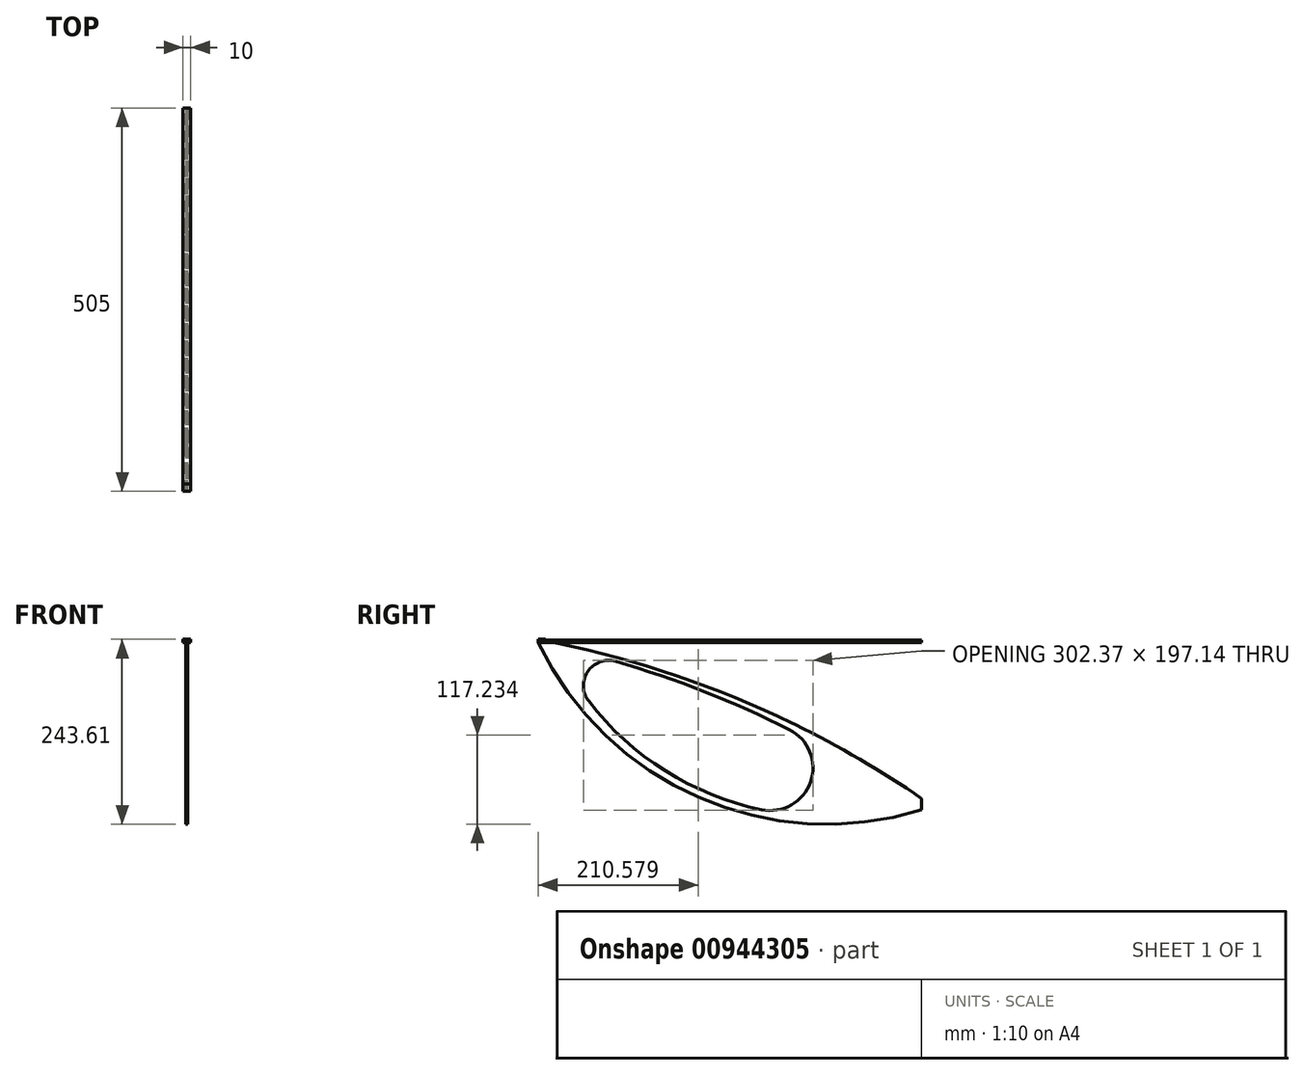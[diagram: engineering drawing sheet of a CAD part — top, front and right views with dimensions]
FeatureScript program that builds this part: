
annotation { "Feature Type Name" : "Feature", "Feature Type Description" : "" }
export const myFeature = defineFeature(function(context is Context, id is Id, definition is map)
    precondition{}
    {
        {
            var Q0;
            Q0=qCreatedBy(makeId("Front.planeOp"),FACE);
            var sketch = newSketch(context, id + "F0", { "sketchPlane" : qUnion([Q0])});
            skLineSegment(sketch, "E0", {"start": v(-5, -10.74) * mm, "end": v(5, -10.74) * mm});
            skLineSegment(sketch, "E1", {"start": v(-5, -7.74) * mm, "end": v(5, -7.74) * mm});
            skLineSegment(sketch, "E2", {"start": v(-5, -7.74) * mm, "end": v(-5, -10.74) * mm});
            skLineSegment(sketch, "E3", {"start": v(5, -7.74) * mm, "end": v(5, -10.74) * mm});
            skSolve(sketch);
        }
        {
            var Q0;
            Q0=makeQuery(id+"F0.imprint","IMPRINT",FACE,{"disambiguationData":[TD([[makeQuery(id+"F0.imprint","IMPRINT",EDGE,{"derivedFrom":sQuery(id+"F0.wireOp",EDGE,"E0")}),1.0]])]});
            var Q1;
            Q1=sQuery(id+"F0.wireOp",EDGE,"E0");
            extrude(context, id + "F1", {"entities" : qUnion([Q0]), "surfaceEntities" : qUnion([Q1]), "depth" : 505 * mm, "offsetDistance" : 25 * mm});
        }
        {
            var Q0;
            Q0=qCreatedBy(makeId("Right.planeOp"),FACE);
            var sketch = newSketch(context, id + "F2", { "sketchPlane" : qUnion([Q0])});
            skArc(sketch, "E4", {"start": v(0, -231.42) * mm, "mid": v(-240.85, -94.43) * mm, "end": v(-505, -10.74) * mm});
            skArc(sketch, "E5", {"start": v(0, -216.42) * mm, "mid": v(-81.58, -164.8) * mm, "end": v(-166.7, -119.23) * mm});
            skLineSegment(sketch, "E6", {"start": v(0, -216.42) * mm, "end": v(0, -231.42) * mm});
            skLineSegment(sketch, "E7", {"start": v(-505, -10.74) * mm, "end": v(-485, -10.74) * mm});
            skLineSegment(sketch, "E8", {"start": v(-170.9, -117.19) * mm, "end": v(-7.33, -10.74) * mm});
            skLineSegment(sketch, "E9", {"start": v(-166.7, -119.23) * mm, "end": v(0, -10.74) * mm});
            skArc(sketch, "E10.trimOffspring", {"start": v(-170.9, -117.19) * mm, "mid": v(-324.61, -54.13) * mm, "end": v(-485, -10.74) * mm});
            skLineSegment(sketch, "E11", {"start": v(0, -10.74) * mm, "end": v(-7.33, -10.74) * mm});
            skPoint(sketch, "E12.orphan", {"position": v(9.17, 0) * mm});
            skLineSegment(sketch, "E13.direction1", {"start": v(-751.48, -1313.77) * mm, "end": v(-726.48, -1313.77) * mm, "construction": true});
            skArc(sketch, "E14.2.0.0", {"start": v(-129.66, -90.36) * mm, "mid": v(-263.2, -43.28) * mm, "end": v(-401, -10.74) * mm});
            skArc(sketch, "E14.2.0.1", {"start": v(-140.93, -97.69) * mm, "mid": v(-281.01, -46.17) * mm, "end": v(-426, -10.74) * mm});
            skArc(sketch, "E15.1.0.0", {"start": v(-119.99, -84.06) * mm, "mid": v(-246.15, -40.95) * mm, "end": v(-376, -10.74) * mm});
            skArc(sketch, "E15.1.0.1", {"start": v(-129.66, -90.36) * mm, "mid": v(-252.57, -46.24) * mm, "end": v(-379.22, -14.45) * mm});
            skArc(sketch, "E15.2.0.0", {"start": v(-110.86, -78.12) * mm, "mid": v(-219.51, -41.32) * mm, "end": v(-330.94, -14.06) * mm});
            skArc(sketch, "E15.2.0.1", {"start": v(-119.99, -84.06) * mm, "mid": v(-235.47, -43.83) * mm, "end": v(-354.18, -14.43) * mm});
            skArc(sketch, "E16.1.0.0", {"start": v(-110.86, -78.12) * mm, "mid": v(-231.58, -35.17) * mm, "end": v(-355.89, -4.09) * mm});
            skArc(sketch, "E17.trimOffspring", {"start": v(-140.93, -97.69) * mm, "mid": v(-277.94, -46.87) * mm, "end": v(-419.72, -11.46) * mm});
            skArc(sketch, "E18.trimOffspring", {"start": v(-78.26, -56.9) * mm, "mid": v(-137.96, -36.17) * mm, "end": v(-198.58, -18.3) * mm});
            skArc(sketch, "E19.trimOffspring", {"start": v(-69.13, -50.96) * mm, "mid": v(-122.21, -33.15) * mm, "end": v(-176, -17.61) * mm});
            skPoint(sketch, "E20.orphan", {"position": v(-226.82, -11.3) * mm});
            skPoint(sketch, "E21.orphan", {"position": v(-178.33, -10.54) * mm});
            skPoint(sketch, "E22.orphan", {"position": v(-151.85, -10.94) * mm});
            skLineSegment(sketch, "E23", {"start": v(-451, -10.74) * mm, "end": v(-476, -10.74) * mm});
            skLineSegment(sketch, "E24", {"start": v(-426, -10.74) * mm, "end": v(-401, -10.74) * mm});
            skLineSegment(sketch, "E25", {"start": v(-376, -10.74) * mm, "end": v(-330.94, -14.06) * mm});
            skLineSegment(sketch, "E26", {"start": v(-151.85, -10.94) * mm, "end": v(-52.05, -39.84) * mm});
            skLineSegment(sketch, "E27", {"start": v(-178.33, -10.54) * mm, "end": v(-59.78, -44.87) * mm});
            skLineSegment(sketch, "E28.1.0.0", {"start": v(-197.9, -117.19) * mm, "end": v(-195.2, -115.43) * mm});
            skLineSegment(sketch, "E28.1.0.1", {"start": v(-193.7, -119.23) * mm, "end": v(-190.56, -117.19) * mm});
            skLineSegment(sketch, "E28.2.0.0", {"start": v(-202.27, -102.46) * mm, "end": v(-173.78, -83.92) * mm});
            skLineSegment(sketch, "E28.2.0.1", {"start": v(-197.96, -104.43) * mm, "end": v(-169.26, -85.75) * mm});
            skLineSegment(sketch, "E28.3.0.0", {"start": v(-218.3, -95.32) * mm, "end": v(-190.57, -77.28) * mm});
            skLineSegment(sketch, "E28.3.0.1", {"start": v(-213.92, -97.25) * mm, "end": v(-185.99, -79.07) * mm});
            skLineSegment(sketch, "E28.4.0.0", {"start": v(-234.56, -88.33) * mm, "end": v(-207.62, -70.8) * mm});
            skLineSegment(sketch, "E28.4.0.1", {"start": v(-230.12, -90.22) * mm, "end": v(-202.97, -72.54) * mm});
            skLineSegment(sketch, "E28.5.0.0", {"start": v(-251.06, -81.5) * mm, "end": v(-224.94, -64.5) * mm});
            skLineSegment(sketch, "E28.5.0.1", {"start": v(-246.56, -83.34) * mm, "end": v(-220.2, -66.2) * mm});
            skLineSegment(sketch, "E28.6.0.0", {"start": v(-267.81, -74.83) * mm, "end": v(-242.53, -58.37) * mm});
            skLineSegment(sketch, "E28.6.0.1", {"start": v(-263.24, -76.63) * mm, "end": v(-237.72, -60.02) * mm});
            skLineSegment(sketch, "E28.7.0.0", {"start": v(-284.82, -68.33) * mm, "end": v(-260.4, -52.43) * mm});
            skLineSegment(sketch, "E28.7.0.1", {"start": v(-280.18, -70.08) * mm, "end": v(-255.51, -54.03) * mm});
            skLineSegment(sketch, "E28.8.0.0", {"start": v(-302.09, -62) * mm, "end": v(-278.56, -46.68) * mm});
            skLineSegment(sketch, "E28.8.0.1", {"start": v(-297.37, -63.7) * mm, "end": v(-273.6, -48.22) * mm});
            skLineSegment(sketch, "E28.9.0.0", {"start": v(-319.62, -55.84) * mm, "end": v(-297.02, -41.13) * mm});
            skLineSegment(sketch, "E28.9.0.1", {"start": v(-314.83, -57.5) * mm, "end": v(-291.98, -42.62) * mm});
            skLineSegment(sketch, "E28.10.0.0", {"start": v(-337.44, -49.86) * mm, "end": v(-315.8, -35.78) * mm});
            skLineSegment(sketch, "E28.10.0.1", {"start": v(-332.57, -51.46) * mm, "end": v(-310.67, -37.2) * mm});
            skLineSegment(sketch, "E28.11.0.0", {"start": v(-355.55, -44.07) * mm, "end": v(-334.9, -30.64) * mm});
            skLineSegment(sketch, "E28.11.0.1", {"start": v(-350.6, -45.62) * mm, "end": v(-329.69, -32.01) * mm});
            skLineSegment(sketch, "E28.12.0.0", {"start": v(-373.95, -38.48) * mm, "end": v(-354.36, -25.72) * mm});
            skLineSegment(sketch, "E28.12.0.1", {"start": v(-368.92, -39.98) * mm, "end": v(-349.04, -27.04) * mm});
            skLineSegment(sketch, "E28.13.0.0", {"start": v(-392.67, -33.09) * mm, "end": v(-374.16, -21.04) * mm});
            skLineSegment(sketch, "E28.13.0.1", {"start": v(-387.55, -34.53) * mm, "end": v(-368.74, -22.29) * mm});
            skLineSegment(sketch, "E28.14.0.0", {"start": v(-411.7, -27.9) * mm, "end": v(-394.33, -16.6) * mm});
            skLineSegment(sketch, "E28.14.0.1", {"start": v(-406.5, -29.29) * mm, "end": v(-388.81, -17.78) * mm});
            skLineSegment(sketch, "E28.15.0.0", {"start": v(-431.08, -22.94) * mm, "end": v(-414.88, -12.4) * mm});
            skLineSegment(sketch, "E28.15.0.1", {"start": v(-425.78, -24.27) * mm, "end": v(-409.26, -13.51) * mm});
            skLineSegment(sketch, "E28.16.0.0", {"start": v(-450.8, -18.2) * mm, "end": v(-439.33, -10.74) * mm});
            skLineSegment(sketch, "E28.16.0.1", {"start": v(-445.4, -19.47) * mm, "end": v(-432, -10.74) * mm});
            skLineSegment(sketch, "E28.direction1", {"start": v(-170.9, -117.19) * mm, "end": v(-197.9, -117.19) * mm, "construction": true});
            skLineSegment(sketch, "E29.trimOffspring", {"start": v(-186.47, -109.75) * mm, "end": v(-157.23, -90.73) * mm});
            skLineSegment(sketch, "E30.trimOffspring", {"start": v(-182.22, -111.76) * mm, "end": v(-152.78, -92.6) * mm});
            skLineSegment(sketch, "E31.trimOffspring", {"start": v(-233.19, -52.3) * mm, "end": v(-225.02, -46.98) * mm});
            skLineSegment(sketch, "E32.trimOffspring", {"start": v(-228.29, -53.88) * mm, "end": v(-220.05, -48.52) * mm});
            skLineSegment(sketch, "E33.trimOffspring", {"start": v(-215.25, -58.2) * mm, "end": v(-206.81, -52.7) * mm});
            skLineSegment(sketch, "E34.trimOffspring", {"start": v(-210.43, -59.83) * mm, "end": v(-201.92, -54.3) * mm});
            skLineSegment(sketch, "E35.trimOffspring", {"start": v(-197.6, -64.28) * mm, "end": v(-188.9, -58.62) * mm});
            skLineSegment(sketch, "E36.trimOffspring", {"start": v(-192.86, -65.97) * mm, "end": v(-184.08, -60.26) * mm});
            skLineSegment(sketch, "E37.trimOffspring", {"start": v(-180.23, -70.54) * mm, "end": v(-171.27, -64.72) * mm});
            skLineSegment(sketch, "E38.trimOffspring", {"start": v(-175.55, -72.28) * mm, "end": v(-166.53, -66.4) * mm});
            skLineSegment(sketch, "E39.trimOffspring", {"start": v(-158.51, -78.76) * mm, "end": v(-149.24, -72.73) * mm});
            skLineSegment(sketch, "E40.trimOffspring", {"start": v(-163.12, -76.98) * mm, "end": v(-153.91, -71) * mm});
            skLineSegment(sketch, "E41.trimOffspring", {"start": v(-146.26, -83.59) * mm, "end": v(-136.82, -77.44) * mm});
            skLineSegment(sketch, "E42.trimOffspring", {"start": v(-141.73, -85.4) * mm, "end": v(-132.22, -79.22) * mm});
            skLineSegment(sketch, "E43.trimOffspring", {"start": v(-251.42, -46.6) * mm, "end": v(-243.54, -41.46) * mm});
            skLineSegment(sketch, "E44.trimOffspring", {"start": v(-246.44, -48.12) * mm, "end": v(-238.48, -42.94) * mm});
            skLineSegment(sketch, "E45.trimOffspring", {"start": v(-269.96, -41.08) * mm, "end": v(-262.37, -36.14) * mm});
            skLineSegment(sketch, "E46.trimOffspring", {"start": v(-264.9, -42.56) * mm, "end": v(-257.22, -37.57) * mm});
            skLineSegment(sketch, "E47.trimOffspring", {"start": v(-288.8, -35.78) * mm, "end": v(-281.52, -31.04) * mm});
            skLineSegment(sketch, "E48.trimOffspring", {"start": v(-283.66, -37.2) * mm, "end": v(-276.29, -32.4) * mm});
            skLineSegment(sketch, "E49.trimOffspring", {"start": v(-308, -30.7) * mm, "end": v(-301.02, -26.16) * mm});
            skLineSegment(sketch, "E50.trimOffspring", {"start": v(-302.75, -32.05) * mm, "end": v(-295.7, -27.46) * mm});
            skLineSegment(sketch, "E51.trimOffspring", {"start": v(-327.52, -25.83) * mm, "end": v(-320.88, -21.5) * mm});
            skLineSegment(sketch, "E52.trimOffspring", {"start": v(-322.18, -27.13) * mm, "end": v(-315.45, -22.75) * mm});
            skLineSegment(sketch, "E53.trimOffspring", {"start": v(-347.4, -21.2) * mm, "end": v(-341.1, -17.1) * mm});
            skLineSegment(sketch, "E54.trimOffspring", {"start": v(-341.96, -22.43) * mm, "end": v(-335.57, -18.27) * mm});
            skLineSegment(sketch, "E55.trimOffspring", {"start": v(-367.65, -16.8) * mm, "end": v(-361.73, -12.95) * mm});
            skLineSegment(sketch, "E56.trimOffspring", {"start": v(-362.12, -17.97) * mm, "end": v(-356.09, -14.05) * mm});
            skLineSegment(sketch, "E57.trimOffspring", {"start": v(-388.3, -12.67) * mm, "end": v(-385.33, -10.74) * mm});
            skLineSegment(sketch, "E58.trimOffspring", {"start": v(-382.66, -13.77) * mm, "end": v(-378, -10.74) * mm});
            skPoint(sketch, "E59.orphan", {"position": v(-405, -10.74) * mm});
            skPoint(sketch, "E60.orphan", {"position": v(-412.33, -10.74) * mm});
            skLineSegment(sketch, "E61.trimOffspring", {"start": v(-127.91, -71.64) * mm, "end": v(-95.53, -50.57) * mm});
            skLineSegment(sketch, "E62.trimOffspring", {"start": v(-123.26, -73.38) * mm, "end": v(-90.81, -52.27) * mm});
            skLineSegment(sketch, "E63.trimOffspring", {"start": v(-145.22, -65.34) * mm, "end": v(-113.08, -44.42) * mm});
            skLineSegment(sketch, "E64.trimOffspring", {"start": v(-140.5, -67.03) * mm, "end": v(-108.29, -46.07) * mm});
            skLineSegment(sketch, "E65.trimOffspring", {"start": v(-162.81, -59.21) * mm, "end": v(-130.9, -38.45) * mm});
            skLineSegment(sketch, "E66.trimOffspring", {"start": v(-158, -60.86) * mm, "end": v(-126.04, -40.05) * mm});
            skLineSegment(sketch, "E67.trimOffspring", {"start": v(-180.68, -53.27) * mm, "end": v(-149.03, -32.67) * mm});
            skLineSegment(sketch, "E68.trimOffspring", {"start": v(-175.8, -54.86) * mm, "end": v(-144.08, -34.22) * mm});
            skLineSegment(sketch, "E69.trimOffspring", {"start": v(-198.84, -47.52) * mm, "end": v(-167.45, -27.08) * mm});
            skLineSegment(sketch, "E70.trimOffspring", {"start": v(-193.88, -49.06) * mm, "end": v(-162.41, -28.58) * mm});
            skLineSegment(sketch, "E71.trimOffspring", {"start": v(-217.3, -41.96) * mm, "end": v(-186.18, -21.7) * mm});
            skLineSegment(sketch, "E72.trimOffspring", {"start": v(-212.26, -43.45) * mm, "end": v(-181.06, -23.14) * mm});
            skLineSegment(sketch, "E73.trimOffspring", {"start": v(-236.08, -36.6) * mm, "end": v(-205.24, -16.53) * mm});
            skLineSegment(sketch, "E74.trimOffspring", {"start": v(-230.95, -38.04) * mm, "end": v(-200.03, -17.92) * mm});
            skLineSegment(sketch, "E75.trimOffspring", {"start": v(-255.19, -31.47) * mm, "end": v(-224.63, -11.58) * mm});
            skLineSegment(sketch, "E76.trimOffspring", {"start": v(-249.96, -32.84) * mm, "end": v(-219.33, -12.9) * mm});
            skLineSegment(sketch, "E77.trimOffspring", {"start": v(-274.63, -26.55) * mm, "end": v(-250.33, -10.74) * mm});
            skLineSegment(sketch, "E78.trimOffspring", {"start": v(-269.31, -27.87) * mm, "end": v(-243, -10.74) * mm});
            skLineSegment(sketch, "E79.trimOffspring", {"start": v(-294.43, -21.86) * mm, "end": v(-277.33, -10.74) * mm});
            skLineSegment(sketch, "E80.trimOffspring", {"start": v(-289.01, -23.11) * mm, "end": v(-270, -10.74) * mm});
            skLineSegment(sketch, "E81.trimOffspring", {"start": v(-314.6, -17.42) * mm, "end": v(-304.33, -10.74) * mm});
            skLineSegment(sketch, "E82.trimOffspring", {"start": v(-309.08, -18.6) * mm, "end": v(-297, -10.74) * mm});
            skPoint(sketch, "E83.orphan", {"position": v(-358.33, -10.74) * mm});
            skPoint(sketch, "E84.orphan", {"position": v(-351, -10.74) * mm});
            skLineSegment(sketch, "E85.trimOffspring", {"start": v(-335.15, -13.22) * mm, "end": v(-331.33, -10.74) * mm});
            skLineSegment(sketch, "E86.trimOffspring", {"start": v(-329.53, -14.34) * mm, "end": v(-324, -10.74) * mm});
            skLineSegment(sketch, "E87.trimOffspring", {"start": v(-86.67, -44.8) * mm, "end": v(-78.47, -39.46) * mm});
            skLineSegment(sketch, "E88.trimOffspring", {"start": v(-81.88, -46.46) * mm, "end": v(-73.4, -40.93) * mm});
            skLineSegment(sketch, "E89.trimOffspring", {"start": v(-104.49, -38.82) * mm, "end": v(-97.15, -34.05) * mm});
            skLineSegment(sketch, "E90.trimOffspring", {"start": v(-99.62, -40.43) * mm, "end": v(-92.08, -35.52) * mm});
            skLineSegment(sketch, "E91.trimOffspring", {"start": v(-141, -27.45) * mm, "end": v(-134.52, -23.23) * mm});
            skLineSegment(sketch, "E92.trimOffspring", {"start": v(-135.97, -28.94) * mm, "end": v(-129.45, -24.7) * mm});
            skLineSegment(sketch, "E93.trimOffspring", {"start": v(-122.6, -33.04) * mm, "end": v(-115.84, -28.64) * mm});
            skLineSegment(sketch, "E94.trimOffspring", {"start": v(-117.65, -34.59) * mm, "end": v(-110.76, -30.11) * mm});
            skLineSegment(sketch, "E95.trimOffspring", {"start": v(-159.72, -22.06) * mm, "end": v(-153.2, -17.82) * mm});
            skLineSegment(sketch, "E96.trimOffspring", {"start": v(-154.6, -23.5) * mm, "end": v(-148.13, -19.29) * mm});
            skLineSegment(sketch, "E97.trimOffspring", {"start": v(-178.76, -16.88) * mm, "end": v(-171.9, -12.4) * mm});
            skLineSegment(sketch, "E98.trimOffspring", {"start": v(-173.56, -18.26) * mm, "end": v(-166.82, -13.88) * mm});
            skLineSegment(sketch, "E99.trimOffspring", {"start": v(-198.15, -11.92) * mm, "end": v(-196.33, -10.74) * mm});
            skLineSegment(sketch, "E100.trimOffspring", {"start": v(-192.85, -13.24) * mm, "end": v(-189, -10.74) * mm});
            skLineSegment(sketch, "E101.trimOffspring", {"start": v(-70.74, -34.43) * mm, "end": v(-34.33, -10.74) * mm});
            skLineSegment(sketch, "E102.trimOffspring", {"start": v(-65.66, -35.9) * mm, "end": v(-27, -10.74) * mm});
            skLineSegment(sketch, "E103.trimOffspring", {"start": v(-89.42, -29.02) * mm, "end": v(-61.33, -10.74) * mm});
            skLineSegment(sketch, "E104.trimOffspring", {"start": v(-84.35, -30.5) * mm, "end": v(-54, -10.74) * mm});
            skLineSegment(sketch, "E105.trimOffspring", {"start": v(-108.11, -23.61) * mm, "end": v(-88.33, -10.74) * mm});
            skLineSegment(sketch, "E106.trimOffspring", {"start": v(-103.04, -25.08) * mm, "end": v(-81, -10.74) * mm});
            skLineSegment(sketch, "E107.trimOffspring", {"start": v(-126.8, -18.2) * mm, "end": v(-115.33, -10.74) * mm});
            skLineSegment(sketch, "E108.trimOffspring", {"start": v(-121.72, -19.67) * mm, "end": v(-108, -10.74) * mm});
            skLineSegment(sketch, "E109.trimOffspring", {"start": v(-145.48, -12.79) * mm, "end": v(-142.33, -10.74) * mm});
            skLineSegment(sketch, "E110.trimOffspring", {"start": v(-140.4, -14.26) * mm, "end": v(-135, -10.74) * mm});
            skLineSegment(sketch, "E111", {"start": v(-176, -17.61) * mm, "end": v(-178.2, -17.02) * mm});
            skLineSegment(sketch, "E112", {"start": v(-198.58, -18.3) * mm, "end": v(-200.93, -17.67) * mm});
            skPoint(sketch, "E113", {"position": v(-200.93, -17.67) * mm});
            skLineSegment(sketch, "E114", {"start": v(-178.2, -17.02) * mm, "end": v(-175.95, -17.67) * mm});
            skLineSegment(sketch, "E115", {"start": v(-177, -17.37) * mm, "end": v(-175.95, -17.67) * mm});
            skLineSegment(sketch, "E116", {"start": v(-200.93, -17.67) * mm, "end": v(-243, -10.74) * mm});
            skLineSegment(sketch, "E117", {"start": v(-243, -10.74) * mm, "end": v(-250.33, -10.74) * mm});
            skLineSegment(sketch, "E118", {"start": v(-270, -10.74) * mm, "end": v(-250.33, -10.74) * mm});
            skLineSegment(sketch, "E119", {"start": v(-297, -10.74) * mm, "end": v(-277.33, -10.74) * mm});
            skLineSegment(sketch, "E120", {"start": v(-270, -10.74) * mm, "end": v(-277.33, -10.74) * mm});
            skLineSegment(sketch, "E121", {"start": v(-324, -10.74) * mm, "end": v(-304.33, -10.74) * mm});
            skLineSegment(sketch, "E122", {"start": v(-324, -10.74) * mm, "end": v(-330.94, -14.06) * mm});
            skLineSegment(sketch, "E123", {"start": v(-376, -10.74) * mm, "end": v(-378, -10.74) * mm});
            skLineSegment(sketch, "E124", {"start": v(-385.33, -10.74) * mm, "end": v(-379.22, -14.45) * mm});
            skLineSegment(sketch, "E125", {"start": v(-385.33, -10.74) * mm, "end": v(-378, -10.74) * mm});
            skLineSegment(sketch, "E126", {"start": v(-426, -10.74) * mm, "end": v(-432, -10.74) * mm});
            skLineSegment(sketch, "E127", {"start": v(-441.95, -10.8) * mm, "end": v(-485, -10.74) * mm});
            skLineSegment(sketch, "E128", {"start": v(-304.33, -10.74) * mm, "end": v(-297, -10.74) * mm});
            skPoint(sketch, "E129", {"position": v(-177, -17.37) * mm});
            skLineSegment(sketch, "E130", {"start": v(-175.95, -17.67) * mm, "end": v(-200.93, -17.67) * mm});
            skPoint(sketch, "E131", {"position": v(-153.94, -10.35) * mm});
            skLineSegment(sketch, "E132", {"start": v(-153.94, -10.35) * mm, "end": v(-178.67, -6.78) * mm});
            skLineSegment(sketch, "E133", {"start": v(-151.85, -10.94) * mm, "end": v(-153.87, -10.36) * mm});
            skLineSegment(sketch, "E134", {"start": v(-178.33, -10.54) * mm, "end": v(-180.35, -9.96) * mm});
            skPoint(sketch, "E135", {"position": v(-180.35, -9.96) * mm});
            skLineSegment(sketch, "E136", {"start": v(-180.35, -9.96) * mm, "end": v(-156.64, -9.96) * mm});
            skLineSegment(sketch, "E137", {"start": v(-180.35, -9.96) * mm, "end": v(-178.2, -17.02) * mm});
            skLineSegment(sketch, "E138", {"start": v(-7.33, -10.74) * mm, "end": v(-153.94, -10.35) * mm});
            skArc(sketch, "E139", {"start": v(-505, -10.74) * mm, "mid": v(-293.58, -215.09) * mm, "end": v(0, -231.42) * mm});
            skArc(sketch, "E140", {"start": v(-485, -10.74) * mm, "mid": v(-289.75, -205.62) * mm, "end": v(-14.34, -221.28) * mm});
            skLineSegment(sketch, "E141", {"start": v(-166.7, -119.23) * mm, "end": v(-170.9, -117.19) * mm});
            skSolve(sketch);
        }
        {
            var Q0;
            {var subQ0=sQuery(id+"F2.wireOp",EDGE,"E139");Q0=makeQuery(id+"F2.imprint","IMPRINT",FACE,{"disambiguationData":[TD([[makeQuery(id+"F2.imprint","IMPRINT",EDGE,{"derivedFrom":subQ0}),1.0]])]});}
            var Q1;
            {var subQ0=sQuery(id+"F2.wireOp",EDGE,"E7");Q1=makeQuery(id+"F2.imprint","IMPRINT",FACE,{"disambiguationData":[TD([[makeQuery(id+"F2.imprint","IMPRINT",EDGE,{"derivedFrom":subQ0}),-1.0]])]});}
            var Q2;
            Q2=makeQuery(id+"F2.imprint","IMPRINT",FACE,{"disambiguationData":[TD([[makeQuery(id+"F2.imprint","IMPRINT",EDGE,{"derivedFrom":sQuery(id+"F2.wireOp",EDGE,"E5")}),1.0]])]});
            extrude(context, id + "F3", {"entities" : qUnion([Q0, Q1, Q2]), "endBound" : BoundingType.SYMMETRIC, "depth" : 2.6 * mm, "offsetDistance" : 25 * mm});
        }
        {
            var Q0;
            Q0=makeQuery(id+"F1.opExtrude","SWEPT_FACE",FACE,{"disambiguationData":[OSD([sQuery(id+"F0.wireOp",EDGE,"E1")])]});
            var sketch = newSketch(context, id + "F4", { "sketchPlane" : qUnion([Q0])});
            skLineSegment(sketch, "E142.bottom", {"start": v(-5, -495.61) * mm, "end": v(5, -495.61) * mm});
            skLineSegment(sketch, "E142.top", {"start": v(-5, -505) * mm, "end": v(5, -505) * mm});
            skLineSegment(sketch, "E142.left", {"start": v(-5, -495.61) * mm, "end": v(-5, -505) * mm});
            skLineSegment(sketch, "E142.right", {"start": v(5, -495.61) * mm, "end": v(5, -505) * mm});
            skSolve(sketch);
        }
        {
            var Q0;
            Q0=makeQuery(id+"F4.imprint","IMPRINT",FACE,{"disambiguationData":[TD([[makeQuery(id+"F4.imprint","IMPRINT",EDGE,{"derivedFrom":sQuery(id+"F4.wireOp",EDGE,"E142.bottom")}),-1.0]])]});
            extrude(context, id + "F5", {"entities" : qUnion([Q0]), "operationType" : NewBodyOperationType.ADD, "depth" : 1 * mm, "offsetDistance" : 25 * mm});
        }
        {
            var Q0;
            {var subQ0=sQuery(id+"F2.wireOp",EDGE,"E140");var subQ1=sQuery(id+"F2.wireOp",EDGE,"E4");Q0=makeQuery(id+"F3.opExtrude","SWEPT_EDGE",EDGE,{"disambiguationData":[OSD([subQ1,subQ0]),TDD([makeQuery(id+"F2.imprint","INTERSECT",VERTEX,{"disambiguationData":[OD(0.0)],"derivedFrom":[subQ1,subQ0]})])]});}
            fillet(context, id + "F6", {"entities" : qUnion([Q0]), "radius" : 56.28 * mm, "tangentPropagation" : true, "allowEdgeOverflow" : false});
        }
        {
            var Q0;
            {var subQ0=sQuery(id+"F2.wireOp",EDGE,"E140");var subQ1=sQuery(id+"F2.wireOp",EDGE,"E4");Q0=makeQuery(id+"F3.opExtrude","SWEPT_EDGE",EDGE,{"disambiguationData":[OSD([subQ1,subQ0]),TDD([makeQuery(id+"F2.imprint","INTERSECT",VERTEX,{"disambiguationData":[OD(1.0)],"derivedFrom":[subQ1,subQ0]})])]});}
            fillet(context, id + "F7", {"entities" : qUnion([Q0]), "radius" : 33.3 * mm, "tangentPropagation" : true, "allowEdgeOverflow" : false});
        }
        {
            var Q0;
            Q0=makeQuery(id+"F3.opExtrude","SWEPT_EDGE",EDGE,{"disambiguationData":[OSD([sQuery(id+"F2.wireOp",EDGE,"E10.trimOffspring"),sQuery(id+"F2.wireOp",EDGE,"E23"),sQuery(id+"F2.wireOp",EDGE,"E127"),sQuery(id+"F2.wireOp",EDGE,"E140")])]});
            fillet(context, id + "F8", {"entities" : qUnion([Q0]), "radius" : 37.3 * mm, "tangentPropagation" : true, "allowEdgeOverflow" : false});
        }
    });
